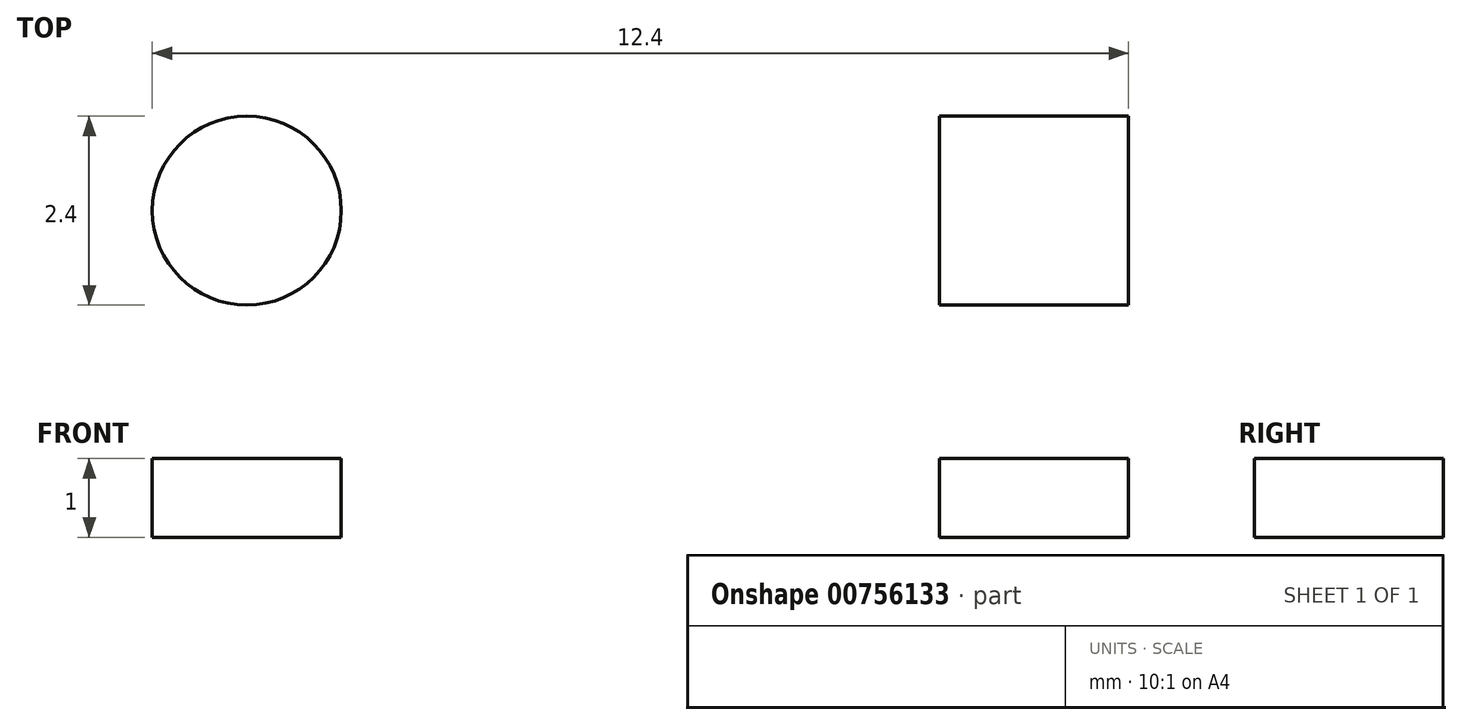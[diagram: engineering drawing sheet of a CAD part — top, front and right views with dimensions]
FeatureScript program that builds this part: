
annotation { "Feature Type Name" : "Feature", "Feature Type Description" : "" }
export const myFeature = defineFeature(function(context is Context, id is Id, definition is map)
    precondition{}
    {
        {
            var Q0;
            Q0=qCreatedBy(makeId("Top.planeOp"),FACE);
            var sketch = newSketch(context, id + "F0", { "sketchPlane" : qUnion([Q0])});
            skCircle(sketch, "E0", {"center": v(0, 0) * mm, "radius": 1.2 * mm});
            skLineSegment(sketch, "E1.bottom", {"start": v(8.8, 1.2) * mm, "end": v(11.2, 1.2) * mm});
            skLineSegment(sketch, "E1.top", {"start": v(8.8, -1.2) * mm, "end": v(11.2, -1.2) * mm});
            skLineSegment(sketch, "E1.left", {"start": v(8.8, 1.2) * mm, "end": v(8.8, -1.2) * mm});
            skLineSegment(sketch, "E1.right", {"start": v(11.2, 1.2) * mm, "end": v(11.2, -1.2) * mm});
            skPoint(sketch, "E1.middle", {"position": v(10, 0) * mm});
            skSolve(sketch);
        }
        {
            var Q0;
            Q0=makeQuery(id+"F0.imprint","IMPRINT",FACE,{"disambiguationData":[TD([[makeQuery(id+"F0.imprint","IMPRINT",EDGE,{"derivedFrom":sQuery(id+"F0.wireOp",EDGE,"E0")}),1.0]])]});
            var Q1;
            Q1=makeQuery(id+"F0.imprint","IMPRINT",FACE,{"disambiguationData":[TD([[makeQuery(id+"F0.imprint","IMPRINT",EDGE,{"derivedFrom":sQuery(id+"F0.wireOp",EDGE,"E1.bottom")}),-1.0]])]});
            extrude(context, id + "F1", {"entities" : qUnion([Q0, Q1]), "depth" : 1 * mm, "offsetDistance" : 25.4 * mm});
        }
    });
